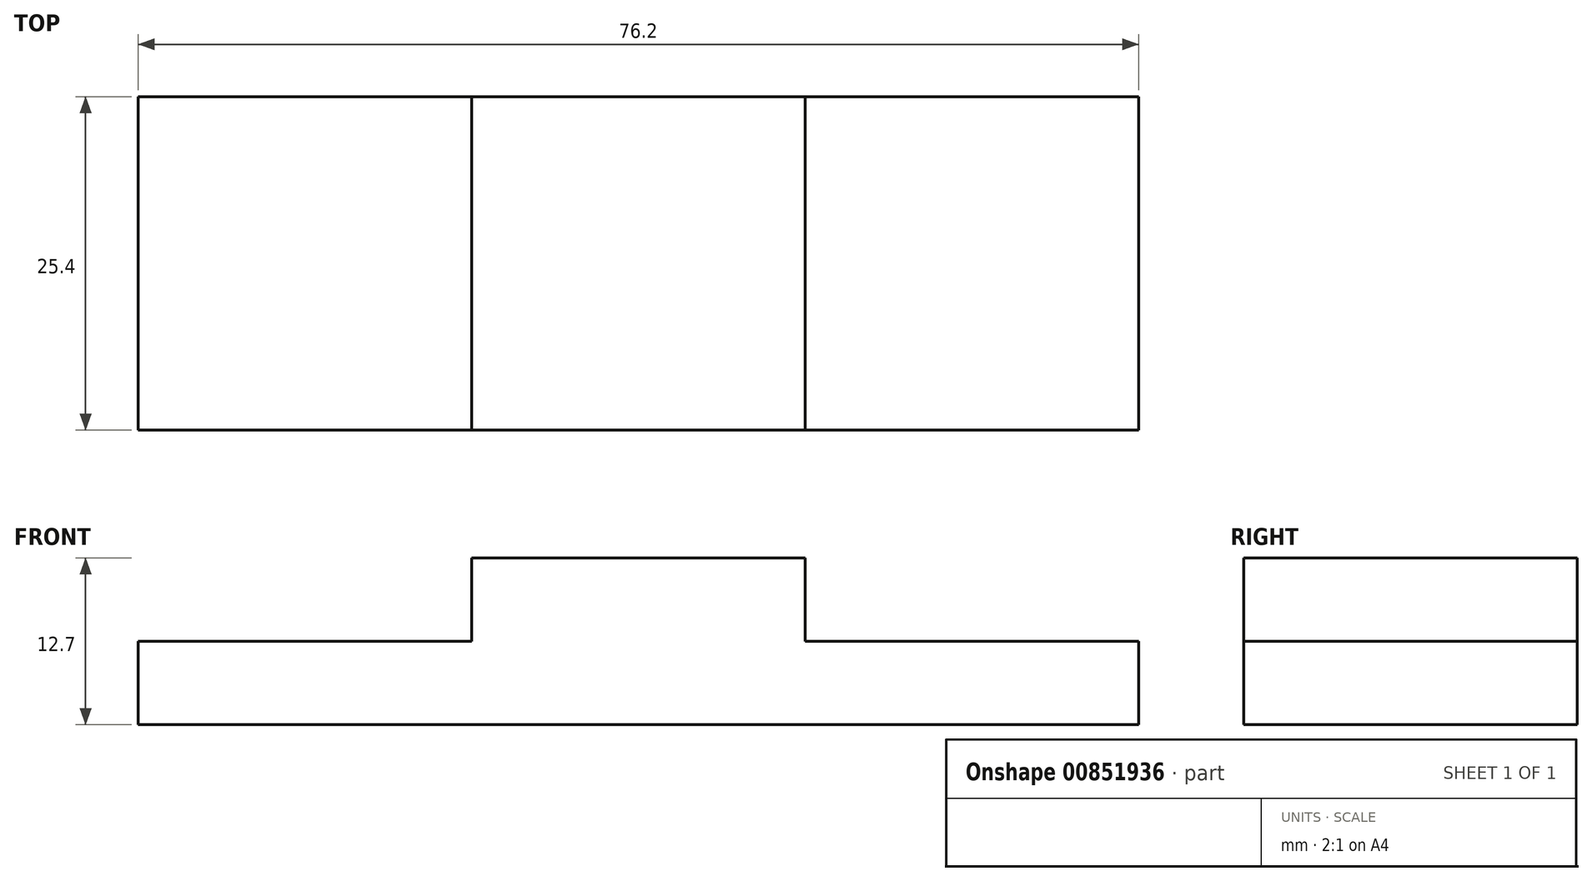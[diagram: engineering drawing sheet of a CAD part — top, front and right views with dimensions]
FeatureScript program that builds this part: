
annotation { "Feature Type Name" : "Feature", "Feature Type Description" : "" }
export const myFeature = defineFeature(function(context is Context, id is Id, definition is map)
    precondition{}
    {
        {
            var Q0;
            Q0=qCreatedBy(makeId("Top.planeOp"),FACE);
            var sketch = newSketch(context, id + "F0", { "sketchPlane" : qUnion([Q0])});
            skLineSegment(sketch, "E0", {"start": v(-45.4, 42.37) * mm, "end": v(30.8, 42.37) * mm});
            skLineSegment(sketch, "E1", {"start": v(30.8, 42.37) * mm, "end": v(30.8, 16.97) * mm});
            skLineSegment(sketch, "E2", {"start": v(30.8, 16.97) * mm, "end": v(-45.4, 16.97) * mm});
            skLineSegment(sketch, "E3", {"start": v(-45.4, 16.97) * mm, "end": v(-45.4, 42.37) * mm});
            skSolve(sketch);
        }
        {
            var Q0;
            Q0=makeQuery(id+"F0.imprint","IMPRINT",FACE,{"disambiguationData":[TD([[makeQuery(id+"F0.imprint","IMPRINT",EDGE,{"derivedFrom":sQuery(id+"F0.wireOp",EDGE,"E0")}),-1.0]])]});
            extrude(context, id + "F1", {"entities" : qUnion([Q0]), "depth" : 6.35 * mm, "offsetDistance" : 25.4 * mm});
        }
        {
            var Q0;
            Q0=makeQuery(id+"F1.opExtrude","CAP_FACE",FACE,{"disambiguationData":[OSD([sQuery(id+"F0.wireOp",EDGE,"E0"),sQuery(id+"F0.wireOp",EDGE,"E1"),sQuery(id+"F0.wireOp",EDGE,"E2"),sQuery(id+"F0.wireOp",EDGE,"E3")])],"isStart":false});
            var sketch = newSketch(context, id + "F2", { "sketchPlane" : qUnion([Q0])});
            skLineSegment(sketch, "E4", {"start": v(5.4, 42.37) * mm, "end": v(5.4, 16.97) * mm});
            skLineSegment(sketch, "E5", {"start": v(5.4, 16.97) * mm, "end": v(-20, 16.97) * mm});
            skLineSegment(sketch, "E6", {"start": v(-20, 16.97) * mm, "end": v(-20, 42.37) * mm});
            skLineSegment(sketch, "E7", {"start": v(-20, 42.37) * mm, "end": v(5.4, 42.37) * mm});
            skSolve(sketch);
        }
        {
            var Q0;
            Q0 = qSketchRegion(id + "F2", true);
            extrude(context, id + "F3", {"entities" : qUnion([Q0]), "operationType" : NewBodyOperationType.ADD, "depth" : 6.35 * mm, "offsetDistance" : 25.4 * mm});
        }
    });
